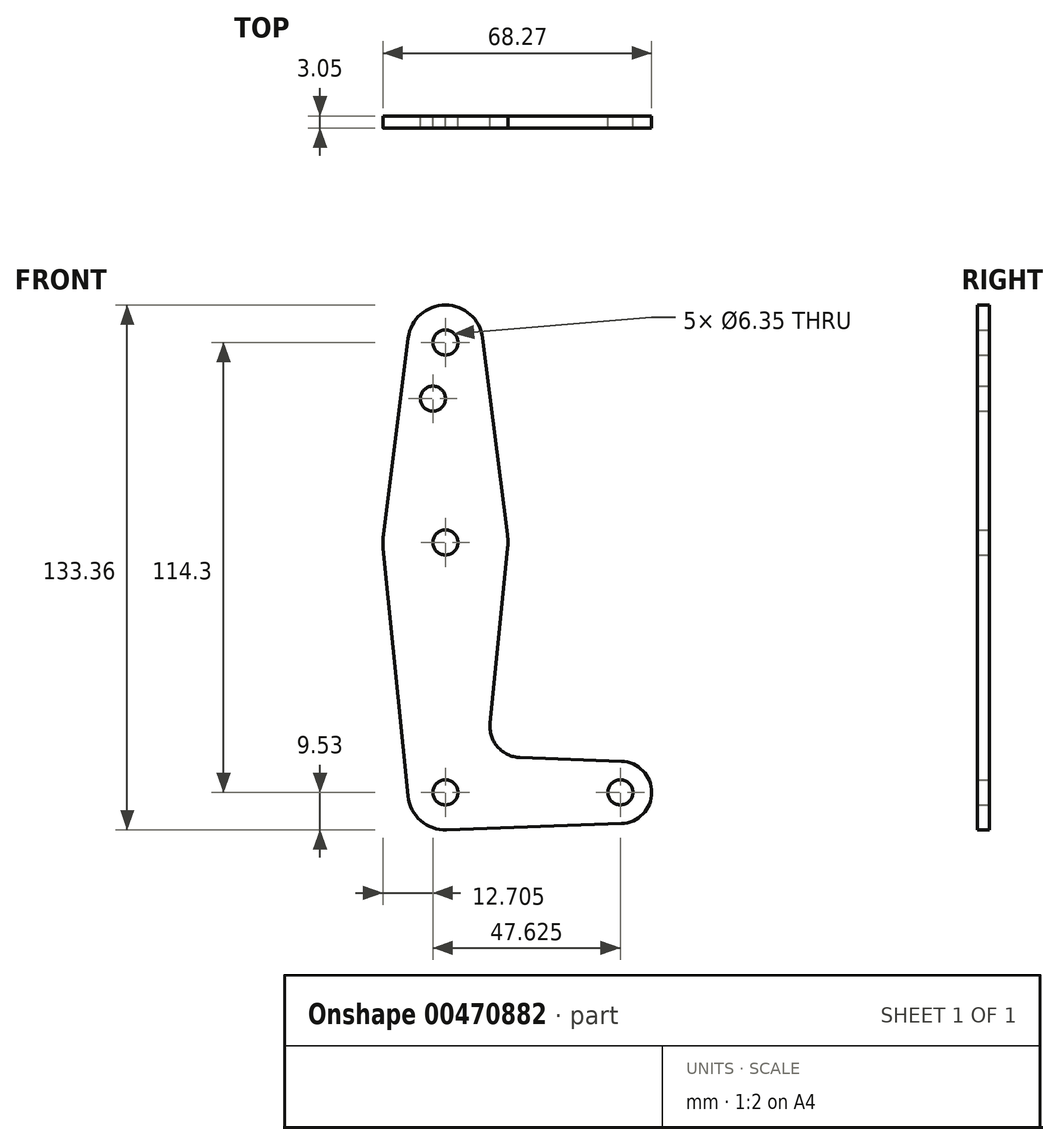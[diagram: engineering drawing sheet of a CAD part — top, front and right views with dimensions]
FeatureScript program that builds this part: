
annotation { "Feature Type Name" : "Feature", "Feature Type Description" : "" }
export const myFeature = defineFeature(function(context is Context, id is Id, definition is map)
    precondition{}
    {
        {
            var Q0;
            Q0=qCreatedBy(makeId("Front.planeOp"),FACE);
            var sketch = newSketch(context, id + "F0", { "sketchPlane" : qUnion([Q0])});
            skCircle(sketch, "E0", {"center": v(0, 0) * mm, "radius": 9.52 * mm});
            skCircle(sketch, "E1", {"center": v(0, -50.8) * mm, "radius": 15.88 * mm});
            skCircle(sketch, "E2", {"center": v(0, -114.3) * mm, "radius": 9.52 * mm});
            skCircle(sketch, "E3", {"center": v(44.45, -114.3) * mm, "radius": 7.94 * mm});
            skLineSegment(sketch, "E4", {"start": v(0, 0) * mm, "end": v(0, -114.3) * mm, "construction": true});
            skLineSegment(sketch, "E5", {"start": v(0, -114.3) * mm, "end": v(44.45, -114.3) * mm, "construction": true});
            skLineSegment(sketch, "E6", {"start": v(-15.75, -48.82) * mm, "end": v(-9.45, 1.2) * mm});
            skLineSegment(sketch, "E7", {"start": v(15.75, -48.82) * mm, "end": v(9.45, 1.2) * mm});
            skLineSegment(sketch, "E8", {"start": v(-15.8, -52.39) * mm, "end": v(-9.48, -115.25) * mm});
            skLineSegment(sketch, "E9", {"start": v(0.34, -123.82) * mm, "end": v(44.73, -122.23) * mm});
            skCircle(sketch, "E10", {"center": v(0, 0) * mm, "radius": 3.18 * mm});
            skCircle(sketch, "E11", {"center": v(-3.17, -14.27) * mm, "radius": 3.18 * mm});
            skCircle(sketch, "E12", {"center": v(0, -50.8) * mm, "radius": 3.18 * mm});
            skCircle(sketch, "E13", {"center": v(0, -114.3) * mm, "radius": 3.18 * mm});
            skCircle(sketch, "E14", {"center": v(44.45, -114.3) * mm, "radius": 3.18 * mm});
            skLineSegment(sketch, "E15", {"start": v(11.34, -96.7) * mm, "end": v(15.8, -52.39) * mm});
            skLineSegment(sketch, "E16", {"start": v(18.97, -105.45) * mm, "end": v(44.73, -106.37) * mm});
            skArc(sketch, "E17.filletArc", {"start": v(11.34, -96.7) * mm, "mid": v(13.26, -102.73) * mm, "end": v(18.97, -105.45) * mm});
            skSolve(sketch);
        }
        {
            var Q0;
            Q0 = qSketchRegion(id + "F0", true);
            extrude(context, id + "F1", {"entities" : qUnion([Q0]), "depth" : 3.05 * mm});
        }
    });
